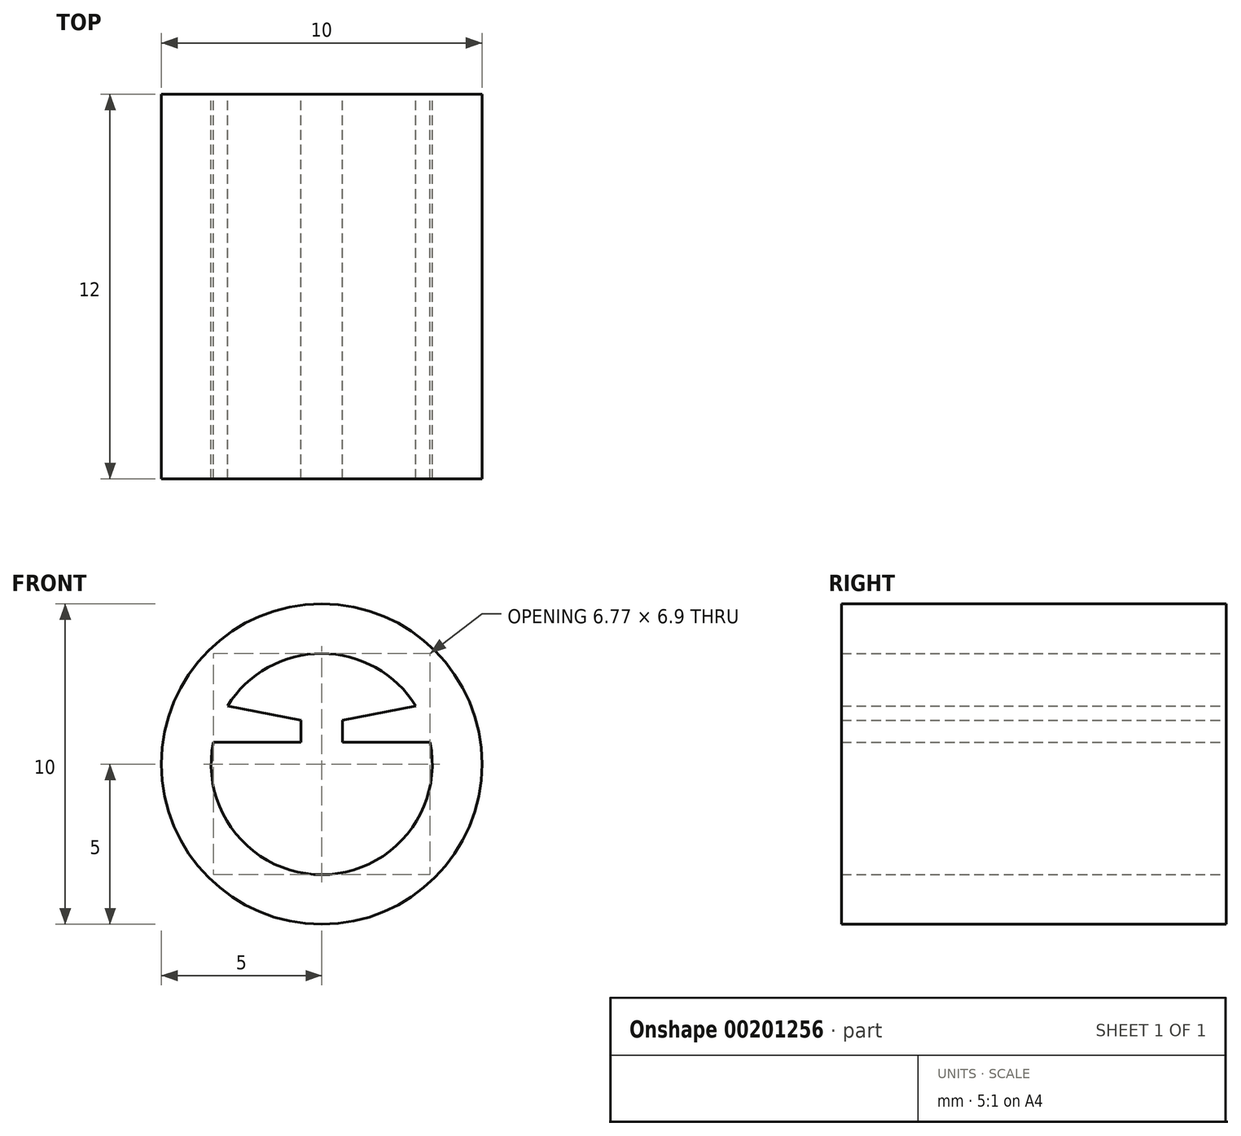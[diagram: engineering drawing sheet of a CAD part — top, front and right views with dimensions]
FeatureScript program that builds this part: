
annotation { "Feature Type Name" : "Feature", "Feature Type Description" : "" }
export const myFeature = defineFeature(function(context is Context, id is Id, definition is map)
    precondition{}
    {
        {
            var Q0;
            Q0=qCreatedBy(makeId("Front.planeOp"),FACE);
            var sketch = newSketch(context, id + "F0", { "sketchPlane" : qUnion([Q0])});
            skCircle(sketch, "E0", {"center": v(0, 0) * mm, "radius": 5 * mm});
            skLineSegment(sketch, "E1", {"start": v(0, -3.5) * mm, "end": v(0, 1) * mm, "construction": true});
            skLineSegment(sketch, "E2", {"start": v(0.65, 0.68) * mm, "end": v(3.38, 0.68) * mm});
            skLineSegment(sketch, "E3", {"start": v(0.65, 0.68) * mm, "end": v(0.65, 1.37) * mm});
            skLineSegment(sketch, "E4", {"start": v(0.65, 1.37) * mm, "end": v(2.94, 1.81) * mm});
            skLineSegment(sketch, "E5.MirrorCS", {"start": v(-0.65, 0.68) * mm, "end": v(-0.65, 1.37) * mm});
            skLineSegment(sketch, "E6.MirrorCS", {"start": v(-0.65, 0.68) * mm, "end": v(-3.38, 0.68) * mm});
            skLineSegment(sketch, "E7.MirrorCS", {"start": v(-0.65, 1.37) * mm, "end": v(-2.94, 1.81) * mm});
            skArc(sketch, "E8", {"start": v(2.94, 1.81) * mm, "mid": v(0, 3.45) * mm, "end": v(-2.94, 1.81) * mm});
            skArc(sketch, "E9.trimOffspring", {"start": v(-3.38, 0.68) * mm, "mid": v(0, -3.45) * mm, "end": v(3.38, 0.68) * mm});
            skSolve(sketch);
        }
        {
            var Q0;
            Q0 = qSketchRegion(id + "F0", true);
            extrude(context, id + "F1", {"entities" : qUnion([Q0]), "depth" : 12 * mm});
        }
    });
